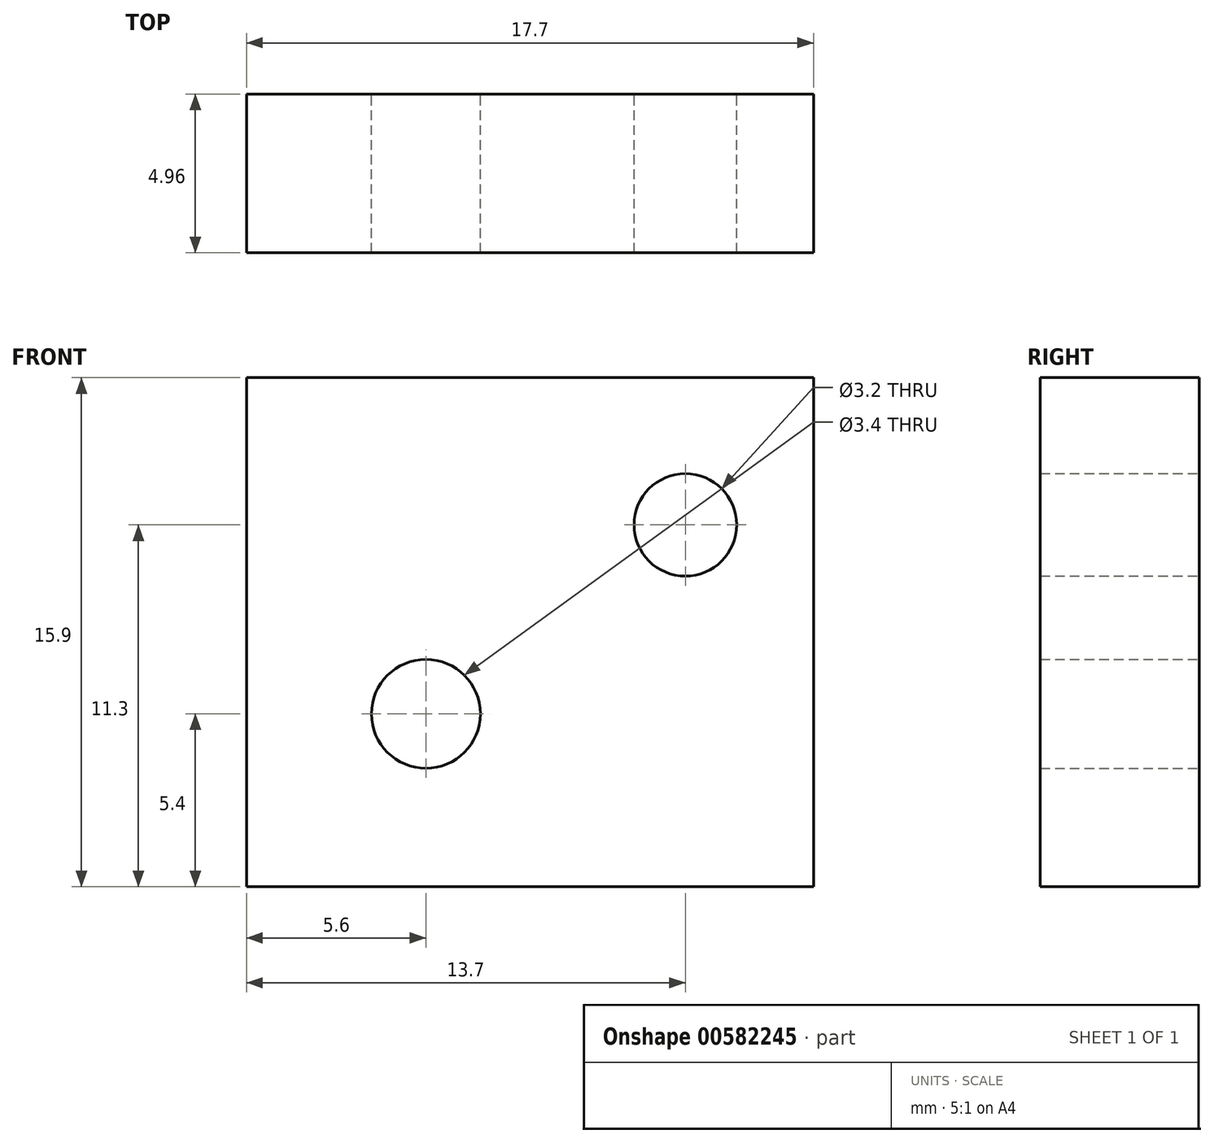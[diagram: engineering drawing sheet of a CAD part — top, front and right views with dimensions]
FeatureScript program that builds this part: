
annotation { "Feature Type Name" : "Feature", "Feature Type Description" : "" }
export const myFeature = defineFeature(function(context is Context, id is Id, definition is map)
    precondition{}
    {
        {
            var Q0;
            Q0=qCreatedBy(makeId("Front.planeOp"),FACE);
            var sketch = newSketch(context, id + "F0", { "sketchPlane" : qUnion([Q0])});
            skLineSegment(sketch, "E0", {"start": v(0, 0) * mm, "end": v(0, 15.9) * mm});
            skLineSegment(sketch, "E1", {"start": v(0, 15.9) * mm, "end": v(-17.7, 15.9) * mm});
            skLineSegment(sketch, "E2", {"start": v(-17.7, 15.9) * mm, "end": v(-17.7, 0) * mm});
            skLineSegment(sketch, "E3", {"start": v(-17.7, 0) * mm, "end": v(0, 0) * mm});
            skCircle(sketch, "E4", {"center": v(-4, 11.3) * mm, "radius": 1.6 * mm});
            skCircle(sketch, "E5", {"center": v(-12.1, 5.4) * mm, "radius": 1.7 * mm});
            skSolve(sketch);
        }
        {
            var Q0;
            Q0 = qSketchRegion(id + "F0", true);
            extrude(context, id + "F1", {"entities" : qUnion([Q0]), "depth" : 4.96 * mm, "offsetDistance" : 25 * mm});
        }
    });
